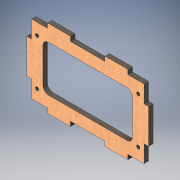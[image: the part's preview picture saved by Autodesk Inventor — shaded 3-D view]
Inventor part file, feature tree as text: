
AUTODESK INVENTOR PART (.ipt)
format: ipt  version: 2019 (Build 230136000, 136)  size: 176,640 bytes
history: native  units: mm
features: sketch x2, other x1, extrude x1, fillet x1, hole x1
ambient origin geometry x8: Origin, YZ Plane, XZ Plane, XY Plane, X Axis, Y Axis, Z Axis, Center Point
bodies: Body1 (feature_tree)
feature tree (6):
  other  "Твердое тело1"
  extrude  "Выдавливание1"  Depth=30.0mm
  fillet  "Сопряжение1"  Radius=4.0mm
  hole  "Отверстие1"  [1 undecoded]
  sketch  "Эскиз1"
  sketch  "Эскиз2"
note: 1 required parameter value undecoded (feature->parameter linkage not recoverable at this tier; creation-order binding heuristic only, values carry confidence <= 0.55)
